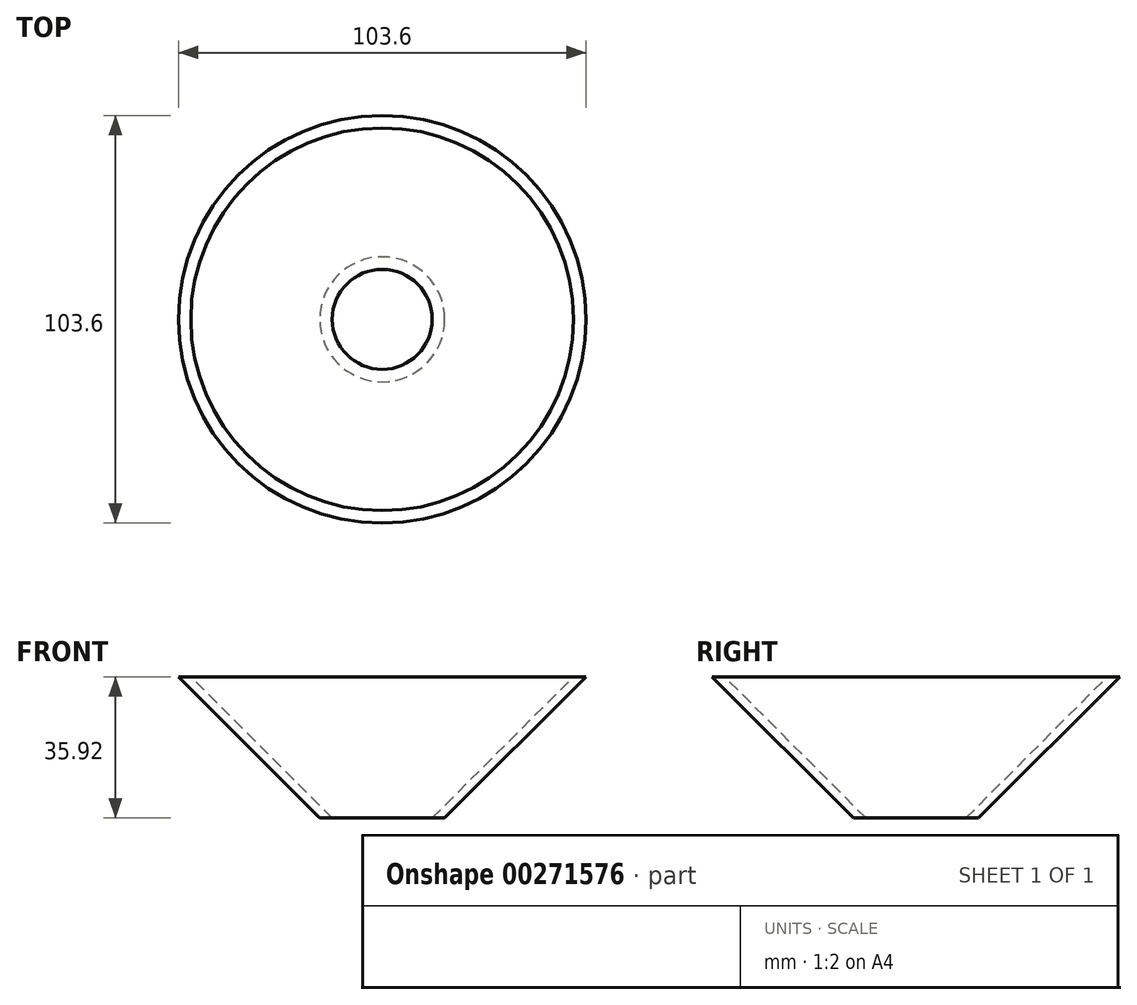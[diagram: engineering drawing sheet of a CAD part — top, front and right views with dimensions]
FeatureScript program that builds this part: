
annotation { "Feature Type Name" : "Feature", "Feature Type Description" : "" }
export const myFeature = defineFeature(function(context is Context, id is Id, definition is map)
    precondition{}
    {
        {
            var Q0;
            Q0=qCreatedBy(makeId("Front.planeOp"),FACE);
            var sketch = newSketch(context, id + "F0", { "sketchPlane" : qUnion([Q0])});
            skLineSegment(sketch, "E0", {"start": v(-48.62, 35.92) * mm, "end": v(-51.8, 35.92) * mm});
            skLineSegment(sketch, "E1", {"start": v(-51.8, 35.92) * mm, "end": v(-15.87, 0) * mm});
            skLineSegment(sketch, "E2", {"start": v(-15.88, 0) * mm, "end": v(-12.7, 0) * mm});
            skLineSegment(sketch, "E3", {"start": v(-12.7, 0) * mm, "end": v(-48.62, 35.92) * mm});
            skLineSegment(sketch, "E4", {"start": v(0, 0) * mm, "end": v(0, 35.92) * mm});
            skSolve(sketch);
        }
        {
            var Q0;
            Q0=makeQuery(id+"F0.imprint","IMPRINT",FACE,{"disambiguationData":[TD([[makeQuery(id+"F0.imprint","IMPRINT",EDGE,{"derivedFrom":sQuery(id+"F0.wireOp",EDGE,"E0")}),1.0]])]});
            var Q1;
            Q1=sQuery(id+"F0.wireOp",EDGE,"E4");
            revolve(context, id + "F1", {"entities" : qUnion([Q0]), "axis" : qUnion([Q1]), "revolveType" : RevolveType.FULL});
        }
    });
